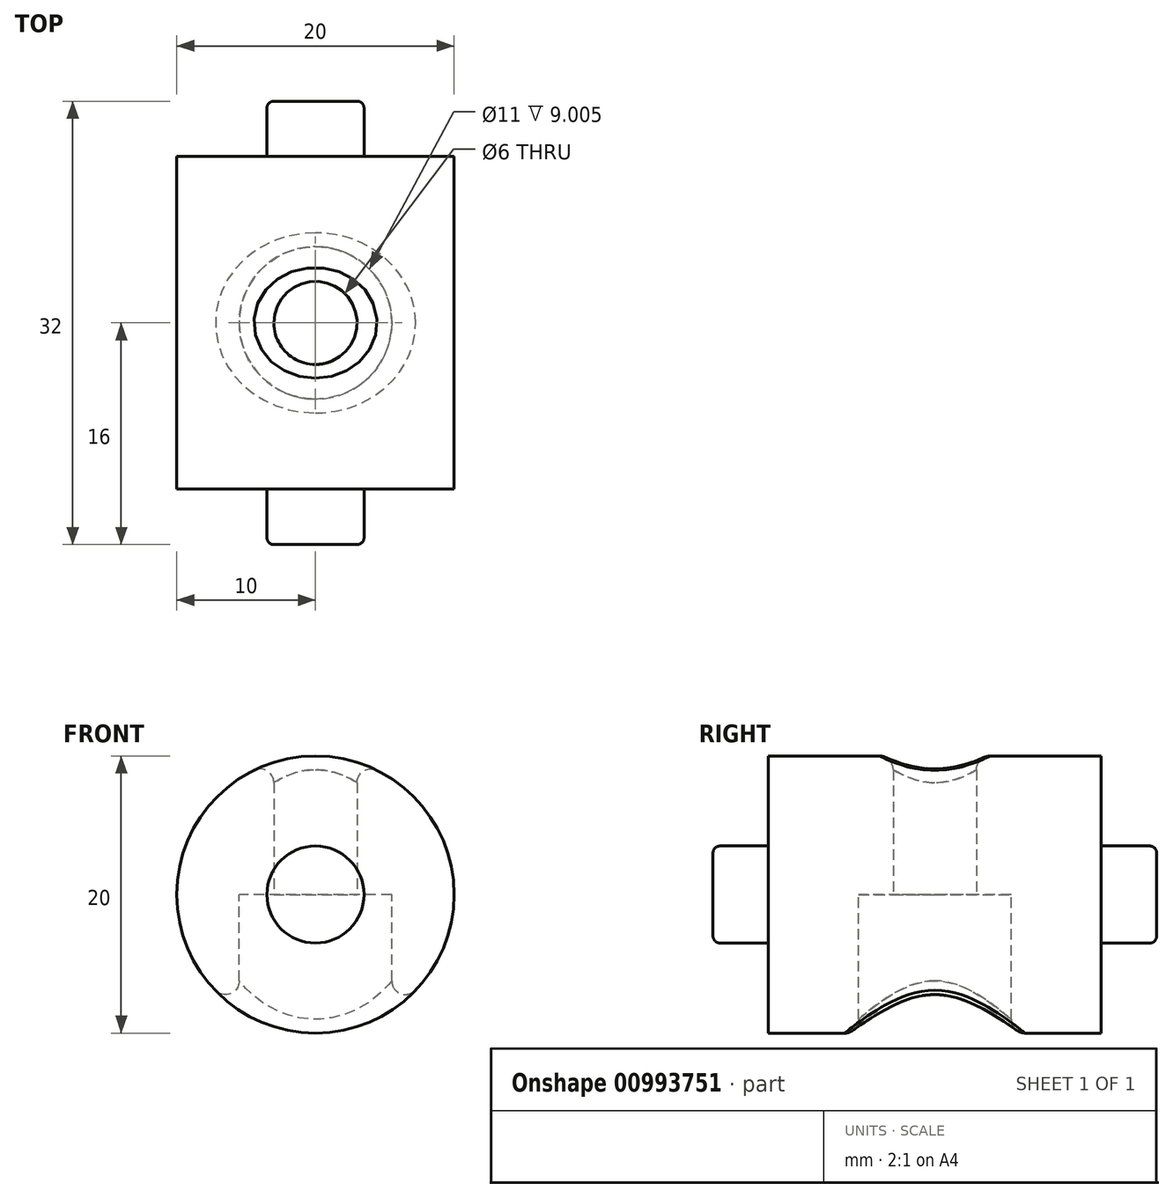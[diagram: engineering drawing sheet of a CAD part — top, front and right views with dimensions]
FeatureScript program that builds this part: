
annotation { "Feature Type Name" : "Feature", "Feature Type Description" : "" }
export const myFeature = defineFeature(function(context is Context, id is Id, definition is map)
    precondition{}
    {
        {
            var Q0;
            Q0=qCreatedBy(makeId("Front.planeOp"),FACE);
            var sketch = newSketch(context, id + "F0", { "sketchPlane" : qUnion([Q0])});
            skCircle(sketch, "E0", {"center": v(0, 0) * mm, "radius": 10 * mm});
            skCircle(sketch, "E1", {"center": v(0, 0) * mm, "radius": 3.5 * mm});
            skSolve(sketch);
        }
        {
            var Q0;
            Q0=makeQuery(id+"F0.imprint","IMPRINT",FACE,{"disambiguationData":[TD([[makeQuery(id+"F0.imprint","IMPRINT",EDGE,{"derivedFrom":sQuery(id+"F0.wireOp",EDGE,"E0")}),1.0]])]});
            var Q1;
            Q1=makeQuery(id+"F0.imprint","IMPRINT",FACE,{"disambiguationData":[TD([[makeQuery(id+"F0.imprint","IMPRINT",EDGE,{"derivedFrom":sQuery(id+"F0.wireOp",EDGE,"E1")}),1.0]])]});
            extrude(context, id + "F1", {"entities" : qUnion([Q0, Q1]), "depth" : 24 * mm, "offsetDistance" : 25 * mm});
        }
        {
            var Q0;
            Q0=qCreatedBy(makeId("Top.planeOp"),FACE);
            var sketch = newSketch(context, id + "F2", { "sketchPlane" : qUnion([Q0])});
            skLineSegment(sketch, "E2", {"start": v(0, 0) * mm, "end": v(0, -12) * mm});
            skCircle(sketch, "E3", {"center": v(0, -12) * mm, "radius": 5.5 * mm});
            skSolve(sketch);
        }
        {
            var Q0;
            Q0=makeQuery(id+"F0.imprint","IMPRINT",FACE,{"disambiguationData":[TD([[makeQuery(id+"F0.imprint","IMPRINT",EDGE,{"derivedFrom":sQuery(id+"F0.wireOp",EDGE,"E1")}),1.0]])]});
            extrude(context, id + "F3", {"entities" : qUnion([Q0]), "operationType" : NewBodyOperationType.ADD, "depth" : 28 * mm, "offsetDistance" : 25 * mm, "hasSecondDirection" : true, "secondDirectionOppositeDirection" : true, "secondDirectionDepth" : 4 * mm});
        }
        {
            var Q0;
            Q0=makeQuery(id+"F2.imprint","IMPRINT",FACE,{"disambiguationData":[TD([[makeQuery(id+"F2.imprint","IMPRINT",EDGE,{"derivedFrom":sQuery(id+"F2.wireOp",EDGE,"E3")}),1.0]])]});
            extrude(context, id + "F4", {"entities" : qUnion([Q0]), "operationType" : NewBodyOperationType.REMOVE, "oppositeDirection" : true, "depth" : 30 * mm, "offsetDistance" : 25 * mm});
        }
        {
            var Q0;
            Q0=makeQuery(id+"F4.boolean.opBoolean","COPY",FACE,{"derivedFrom":makeQuery(id+"F4.opExtrude","CAP_FACE",FACE,{"disambiguationData":[OSD([sQuery(id+"F2.wireOp",EDGE,"E3")])],"isStart":true})});
            var sketch = newSketch(context, id + "F5", { "sketchPlane" : qUnion([Q0])});
            skPoint(sketch, "E4", {"position": v(0, 12) * mm});
            skCircle(sketch, "E5", {"center": v(0, 12) * mm, "radius": 3 * mm});
            skSolve(sketch);
        }
        {
            var Q0;
            Q0=makeQuery(id+"F5.imprint","IMPRINT",FACE,{"disambiguationData":[TD([[makeQuery(id+"F5.imprint","IMPRINT",EDGE,{"derivedFrom":sQuery(id+"F5.wireOp",EDGE,"E5")}),1.0]])]});
            extrude(context, id + "F6", {"entities" : qUnion([Q0]), "operationType" : NewBodyOperationType.REMOVE, "endBound" : BoundingType.THROUGH_ALL, "oppositeDirection" : true, "depth" : 25 * mm, "offsetDistance" : 25 * mm});
        }
        {
            var Q0;
            Q0=makeQuery(id+"F3.opExtrude","CAP_FACE",FACE,{"disambiguationData":[OSD([sQuery(id+"F0.wireOp",EDGE,"E1")])],"isStart":false});
            var Q1;
            Q1=makeQuery(id+"F3.opExtrude","CAP_EDGE",EDGE,{"disambiguationData":[OSD([sQuery(id+"F0.wireOp",EDGE,"E1")])],"isStart":true});
            fillet(context, id + "F7", {"entities" : qUnion([Q0, Q1]), "radius" : 0.5 * mm, "tangentPropagation" : true, "allowEdgeOverflow" : false});
        }
        {
            var Q0;
            Q0=makeQuery(id+"F6.boolean.opBoolean","INTERSECT",EDGE,{"derivedFrom":[makeQuery(id+"F1.opExtrude","SWEPT_FACE",FACE,{"disambiguationData":[OSD([sQuery(id+"F0.wireOp",EDGE,"E0")])]}),makeQuery(id+"F6.opExtrude","SWEPT_FACE",FACE,{"disambiguationData":[OSD([sQuery(id+"F5.wireOp",EDGE,"E5")])]})]});
            var Q1;
            Q1=makeQuery(id+"F4.boolean.opBoolean","INTERSECT",EDGE,{"derivedFrom":[makeQuery(id+"F1.opExtrude","SWEPT_FACE",FACE,{"disambiguationData":[OSD([sQuery(id+"F0.wireOp",EDGE,"E0")])]}),makeQuery(id+"F4.opExtrude","SWEPT_FACE",FACE,{"disambiguationData":[OSD([sQuery(id+"F2.wireOp",EDGE,"E3")])]})]});
            fillet(context, id + "F8", {"entities" : qUnion([Q0, Q1]), "radius" : 1 * mm, "tangentPropagation" : true, "allowEdgeOverflow" : false});
        }
    });
